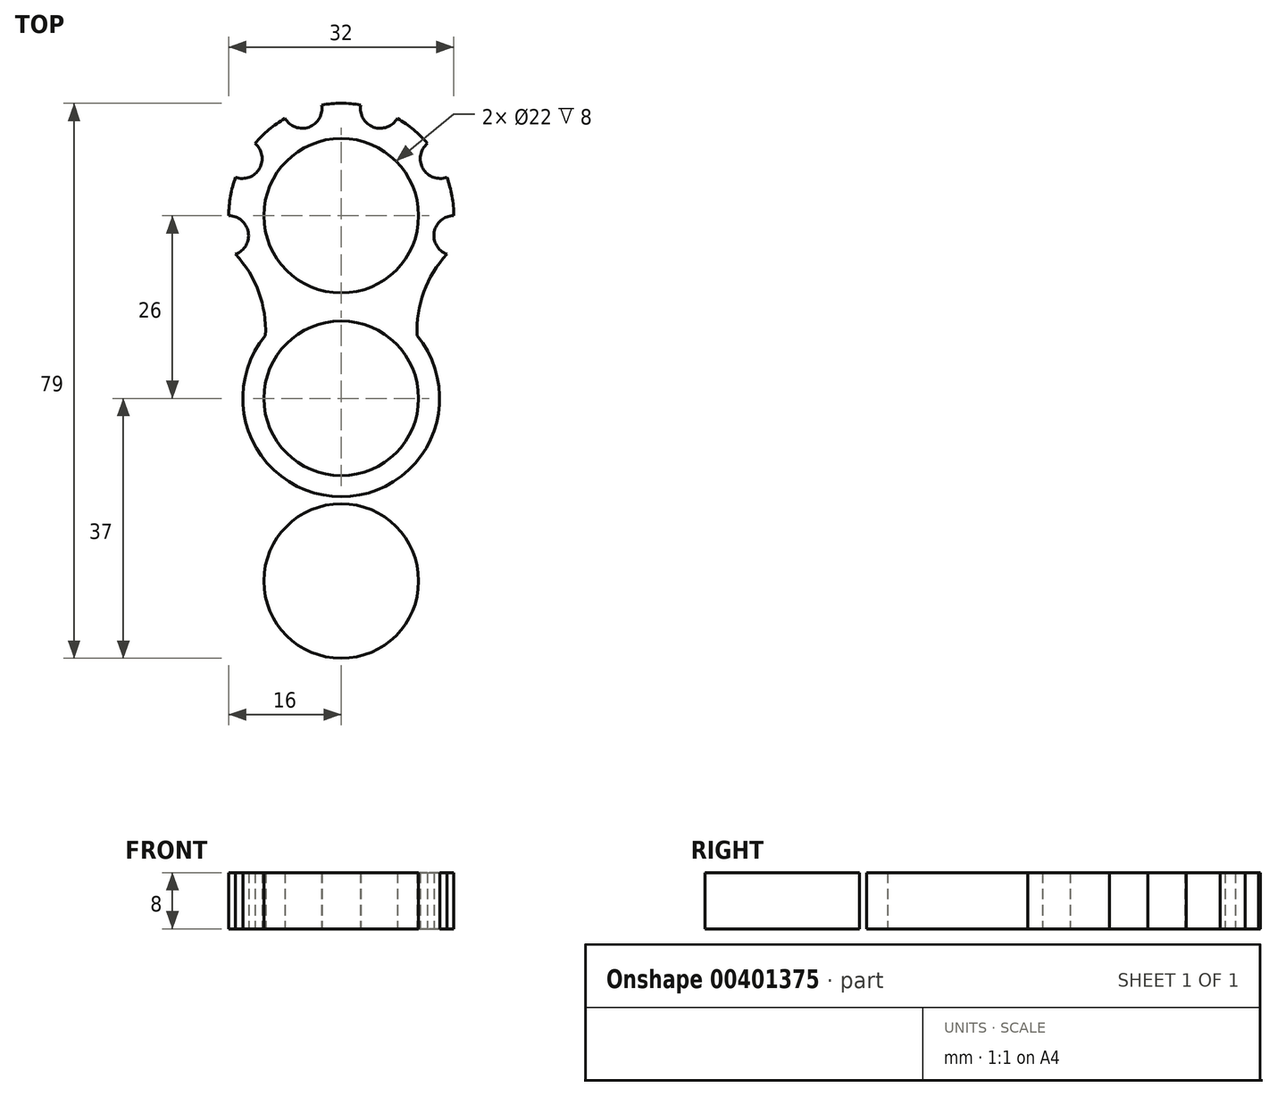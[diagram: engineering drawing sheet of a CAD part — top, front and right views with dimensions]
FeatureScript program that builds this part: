
annotation { "Feature Type Name" : "Feature", "Feature Type Description" : "" }
export const myFeature = defineFeature(function(context is Context, id is Id, definition is map)
    precondition{}
    {
        {
            var Q0;
            Q0=qCreatedBy(makeId("Top.planeOp"),FACE);
            var sketch = newSketch(context, id + "F0", { "sketchPlane" : qUnion([Q0])});
            skCircle(sketch, "E0", {"center": v(0, 0) * mm, "radius": 11 * mm});
            skCircle(sketch, "E1", {"center": v(0, 26) * mm, "radius": 11 * mm});
            skCircle(sketch, "E2.0", {"center": v(0, 0) * mm, "radius": 14 * mm});
            skPoint(sketch, "E3", {"position": v(-14, 0) * mm});
            skLineSegment(sketch, "E4", {"start": v(-15.04, 20.53) * mm, "end": v(0, 26) * mm, "construction": true});
            skLineSegment(sketch, "E5.MirrorCS", {"start": v(15.04, 20.53) * mm, "end": v(0, 26) * mm, "construction": true});
            skLineSegment(sketch, "E6", {"start": v(-14, 0) * mm, "end": v(-14, 0) * mm});
            skLineSegment(sketch, "E7.MirrorCS", {"start": v(14, 0) * mm, "end": v(14, 0) * mm});
            skArc(sketch, "E8", {"start": v(10.78, 8.93) * mm, "mid": v(10.95, 12.07) * mm, "end": v(11.73, 15.12) * mm});
            skArc(sketch, "E9", {"start": v(-10.78, 8.93) * mm, "mid": v(-10.95, 12.07) * mm, "end": v(-11.73, 15.12) * mm});
            skArc(sketch, "E10", {"start": v(-11.73, 15.12) * mm, "mid": v(-13.11, 17.99) * mm, "end": v(-15.04, 20.53) * mm});
            skArc(sketch, "E11", {"start": v(11.73, 15.12) * mm, "mid": v(13.11, 17.99) * mm, "end": v(15.04, 20.53) * mm});
            skArc(sketch, "E12", {"start": v(15.04, 20.53) * mm, "mid": v(0, 42) * mm, "end": v(-15.04, 20.53) * mm});
            skCircle(sketch, "E13.MirrorC", {"center": v(0, -26) * mm, "radius": 11 * mm});
            skArc(sketch, "E14.MirrorCS", {"start": v(15.04, -20.53) * mm, "mid": v(0, -42) * mm, "end": v(-15.04, -20.53) * mm});
            skArc(sketch, "E15.MirrorCS", {"start": v(-11.73, -15.12) * mm, "mid": v(-13.11, -17.99) * mm, "end": v(-15.04, -20.53) * mm});
            skArc(sketch, "E16.MirrorCS", {"start": v(-10.78, -8.93) * mm, "mid": v(-10.95, -12.07) * mm, "end": v(-11.73, -15.12) * mm});
            skArc(sketch, "E17.MirrorCS", {"start": v(10.78, -8.93) * mm, "mid": v(10.95, -12.07) * mm, "end": v(11.73, -15.12) * mm});
            skArc(sketch, "E18.MirrorCS", {"start": v(11.73, -15.12) * mm, "mid": v(13.11, -17.99) * mm, "end": v(15.04, -20.53) * mm});
            skLineSegment(sketch, "E19", {"start": v(0, 26) * mm, "end": v(-16, 26) * mm, "construction": true});
            skArc(sketch, "E20", {"start": v(-15.04, 20.53) * mm, "mid": v(-13.22, 23.67) * mm, "end": v(-16, 26) * mm});
            skArc(sketch, "E21.1.0", {"start": v(-15.04, 31.47) * mm, "mid": v(-11.63, 32.71) * mm, "end": v(-12.26, 36.28) * mm});
            skArc(sketch, "E21.2.0", {"start": v(-8, 39.86) * mm, "mid": v(-4.6, 38.62) * mm, "end": v(-2.78, 41.76) * mm});
            skArc(sketch, "E21.3.0", {"start": v(2.78, 41.76) * mm, "mid": v(4.6, 38.62) * mm, "end": v(8, 39.86) * mm});
            skArc(sketch, "E21.4.0", {"start": v(12.26, 36.28) * mm, "mid": v(11.63, 32.71) * mm, "end": v(15.04, 31.47) * mm});
            skArc(sketch, "E21.5.0", {"start": v(16, 26) * mm, "mid": v(13.22, 23.67) * mm, "end": v(15.04, 20.53) * mm});
            skLineSegment(sketch, "E21.anchor1", {"start": v(0, 26) * mm, "end": v(-15.04, 20.53) * mm, "construction": true});
            skLineSegment(sketch, "E21.anchor2", {"start": v(0, 26) * mm, "end": v(16, 26) * mm, "construction": true});
            skArc(sketch, "E22.MirrorCS", {"start": v(-15.04, -20.53) * mm, "mid": v(-13.22, -23.67) * mm, "end": v(-16, -26) * mm});
            skArc(sketch, "E23.MirrorCS", {"start": v(-15.04, -31.47) * mm, "mid": v(-11.63, -32.71) * mm, "end": v(-12.26, -36.28) * mm});
            skArc(sketch, "E24.MirrorCS", {"start": v(-8, -39.86) * mm, "mid": v(-4.6, -38.62) * mm, "end": v(-2.78, -41.76) * mm});
            skArc(sketch, "E25.MirrorCS", {"start": v(2.78, -41.76) * mm, "mid": v(4.6, -38.62) * mm, "end": v(8, -39.86) * mm});
            skArc(sketch, "E26.MirrorCS", {"start": v(12.26, -36.28) * mm, "mid": v(11.63, -32.71) * mm, "end": v(15.04, -31.47) * mm});
            skArc(sketch, "E27.MirrorCS", {"start": v(16, -26) * mm, "mid": v(13.22, -23.67) * mm, "end": v(15.04, -20.53) * mm});
            skSolve(sketch);
        }
        {
            var Q0;
            Q0=makeQuery(id+"F0.imprint","IMPRINT",FACE,{"disambiguationData":[TD([[makeQuery(id+"F0.imprint","IMPRINT",EDGE,{"derivedFrom":sQuery(id+"F0.wireOp",EDGE,"E1")}),-1.0]])]});
            var Q1;
            Q1=makeQuery(id+"F0.imprint","IMPRINT",FACE,{"disambiguationData":[TD([[makeQuery(id+"F0.imprint","IMPRINT",EDGE,{"derivedFrom":sQuery(id+"F0.wireOp",EDGE,"E0")}),-1.0]])]});
            var Q2;
            Q2=makeQuery(id+"F0.imprint","IMPRINT",FACE,{"disambiguationData":[TD([[makeQuery(id+"F0.imprint","IMPRINT",EDGE,{"derivedFrom":sQuery(id+"F0.wireOp",EDGE,"E13.MirrorC")}),1.0]])]});
            extrude(context, id + "F1", {"entities" : qUnion([Q0, Q1, Q2]), "depth" : 8 * mm});
        }
    });
